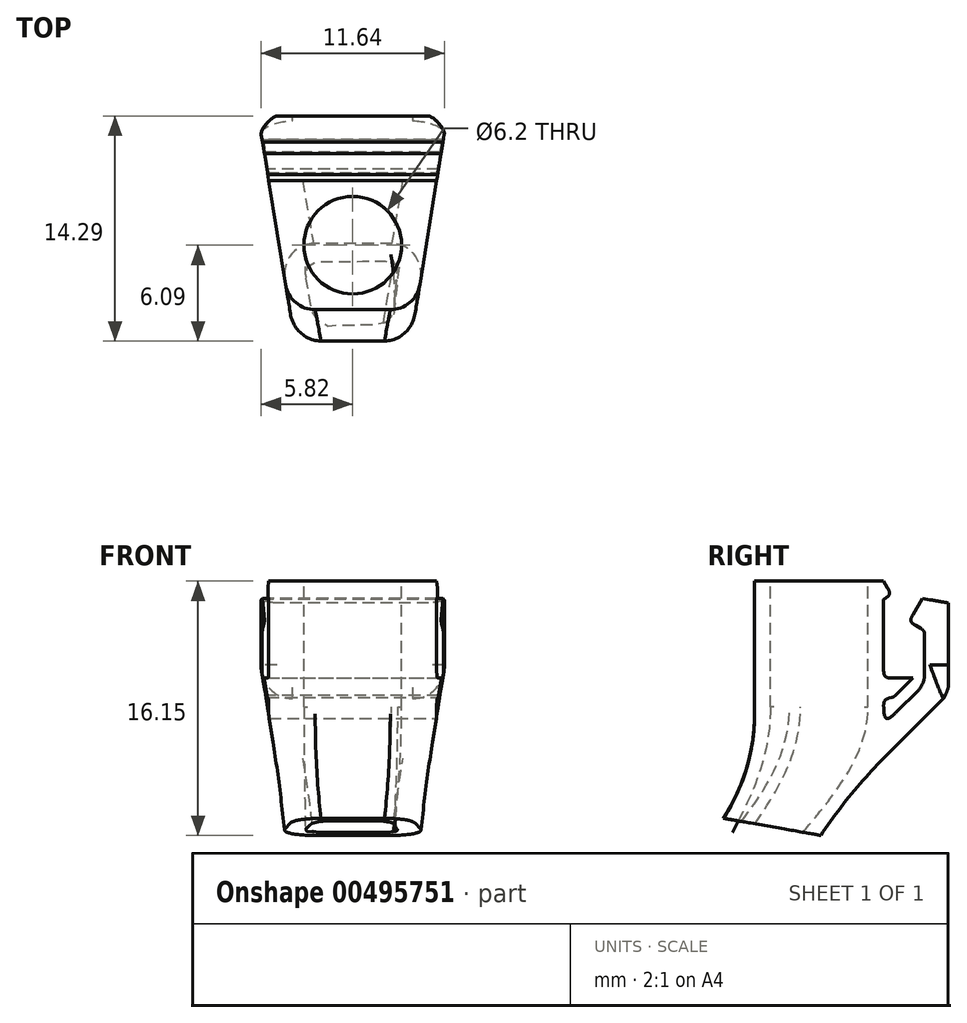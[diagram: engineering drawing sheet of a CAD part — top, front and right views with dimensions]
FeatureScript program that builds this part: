
annotation { "Feature Type Name" : "Feature", "Feature Type Description" : "" }
export const myFeature = defineFeature(function(context is Context, id is Id, definition is map)
    precondition{}
    {
        {
            var Q0;
            Q0=qCreatedBy(makeId("Right.planeOp"),FACE);
            var sketch = newSketch(context, id + "F0", { "sketchPlane" : qUnion([Q0])});
            skLineSegment(sketch, "E0", {"start": v(0, 0) * mm, "end": v(7, 0) * mm});
            skLineSegment(sketch, "E1", {"start": v(15.1, 9) * mm, "end": v(15.1, 14.77) * mm});
            skLineSegment(sketch, "E2", {"start": v(13.45, 15.06) * mm, "end": v(12.6, 13.58) * mm});
            skLineSegment(sketch, "E3", {"start": v(12.6, 13.58) * mm, "end": v(13.6, 13) * mm});
            skLineSegment(sketch, "E4", {"start": v(13.6, 13) * mm, "end": v(13.6, 10) * mm});
            skLineSegment(sketch, "E5", {"start": v(13.6, 10) * mm, "end": v(11, 10) * mm});
            skLineSegment(sketch, "E6", {"start": v(11, 10) * mm, "end": v(11, 15) * mm});
            skLineSegment(sketch, "E7", {"start": v(11, 15) * mm, "end": v(11.5, 15.29) * mm});
            skLineSegment(sketch, "E8", {"start": v(11.5, 15.29) * mm, "end": v(11, 16.15) * mm});
            skLineSegment(sketch, "E9", {"start": v(11, 16.15) * mm, "end": v(2.8, 16.15) * mm});
            skLineSegment(sketch, "E10", {"start": v(2.8, 16.15) * mm, "end": v(0, 0) * mm, "construction": true});
            skLineSegment(sketch, "E11", {"start": v(2.8, 16.15) * mm, "end": v(2.8, 7.7) * mm});
            skArc(sketch, "E12", {"start": v(0, 0) * mm, "mid": v(2.08, 3.6) * mm, "end": v(2.8, 7.7) * mm});
            skLineSegment(sketch, "E13", {"start": v(15.1, 9) * mm, "end": v(11, 4.9) * mm});
            skArc(sketch, "E14", {"start": v(7, 0) * mm, "mid": v(8.88, 2.54) * mm, "end": v(11, 4.9) * mm});
            skLineSegment(sketch, "E15", {"start": v(13.45, 15.06) * mm, "end": v(15.1, 14.77) * mm});
            skSolve(sketch);
        }
        {
            var Q0;
            Q0=qSketchRegion(id+"F0",true);
            extrude(context, id + "F1", {"entities" : qUnion([Q0]), "endBound" : BoundingType.SYMMETRIC, "depth" : 12 * mm});
        }
        {
            var Q0;
            Q0=qCreatedBy(makeId("Right.planeOp"),FACE);
            var sketch = newSketch(context, id + "F2", { "sketchPlane" : qUnion([Q0])});
            skLineSegment(sketch, "E16", {"start": v(13.6, 9.62) * mm, "end": v(11, 7.02) * mm});
            skLineSegment(sketch, "E17", {"start": v(11, 7.02) * mm, "end": v(11, 8.63) * mm});
            skLineSegment(sketch, "E18", {"start": v(11, 8.63) * mm, "end": v(11.65, 8.8) * mm});
            skLineSegment(sketch, "E19", {"start": v(11.65, 8.8) * mm, "end": v(12.85, 10) * mm});
            skLineSegment(sketch, "E20", {"start": v(12.85, 10) * mm, "end": v(13.6, 10) * mm});
            skLineSegment(sketch, "E21", {"start": v(13.6, 9.62) * mm, "end": v(13.6, 10) * mm});
            skSolve(sketch);
        }
        {
            var Q0;
            Q0=qSketchRegion(id+"F2",true);
            extrude(context, id + "F3", {"entities" : qUnion([Q0]), "operationType" : NewBodyOperationType.REMOVE, "endBound" : BoundingType.THROUGH_ALL, "oppositeDirection" : true, "depth" : 25 * mm, "hasSecondDirection" : true, "secondDirectionBound" : SecondDirectionBoundingType.THROUGH_ALL, "secondDirectionOppositeDirection" : false, "secondDirectionDepth" : 25 * mm});
        }
        {
            var Q0;
            Q0=makeQuery(id+"F1.opExtrude","SWEPT_FACE",FACE,{"disambiguationData":[OSD([sQuery(id+"F0.wireOp",EDGE,"E9")])]});
            var sketch = newSketch(context, id + "F4", { "sketchPlane" : qUnion([Q0])});
            skLineSegment(sketch, "E22", {"start": v(-6, 15.1) * mm, "end": v(-4, 2.8) * mm});
            skLineSegment(sketch, "E23", {"start": v(-4, 2.8) * mm, "end": v(-6, 2.8) * mm});
            skLineSegment(sketch, "E24", {"start": v(-6, 2.8) * mm, "end": v(-6, 15.1) * mm});
            skLineSegment(sketch, "E25", {"start": v(6, 2.8) * mm, "end": v(4, 2.8) * mm});
            skLineSegment(sketch, "E26", {"start": v(4, 2.8) * mm, "end": v(6, 15.1) * mm});
            skLineSegment(sketch, "E27", {"start": v(6, 15.1) * mm, "end": v(6, 2.8) * mm});
            skLineSegment(sketch, "E28", {"start": v(-4, 2.8) * mm, "end": v(-3.54, 0) * mm});
            skLineSegment(sketch, "E29", {"start": v(-3.54, 0) * mm, "end": v(-6, 0) * mm});
            skLineSegment(sketch, "E30", {"start": v(-6, 0) * mm, "end": v(-6, 2.8) * mm});
            skLineSegment(sketch, "E31", {"start": v(6, 2.8) * mm, "end": v(6, 0) * mm});
            skLineSegment(sketch, "E32", {"start": v(6, 0) * mm, "end": v(3.54, 0) * mm});
            skLineSegment(sketch, "E33", {"start": v(3.54, 0) * mm, "end": v(4, 2.8) * mm});
            skSolve(sketch);
        }
        {
            var Q0;
            Q0=qSketchRegion(id+"F4",true);
            extrude(context, id + "F5", {"entities" : qUnion([Q0]), "operationType" : NewBodyOperationType.REMOVE, "endBound" : BoundingType.THROUGH_ALL, "oppositeDirection" : true, "depth" : 25 * mm});
        }
        {
            var Q0;
            Q0=makeQuery(id+"F5.boolean.opBoolean","INTERSECT",EDGE,{"derivedFrom":[makeQuery(id+"F1.opExtrude","SWEPT_FACE",FACE,{"disambiguationData":[OSD([sQuery(id+"F0.wireOp",EDGE,"E14")])]}),makeQuery(id+"F5.opExtrude","SWEPT_FACE",FACE,{"disambiguationData":[OSD([sQuery(id+"F4.wireOp",EDGE,"E22"),sQuery(id+"F4.wireOp",EDGE,"E28")])]})]});
            var Q1;
            Q1=makeQuery(id+"F5.boolean.opBoolean","INTERSECT",EDGE,{"derivedFrom":[makeQuery(id+"F1.opExtrude","SWEPT_FACE",FACE,{"disambiguationData":[OSD([sQuery(id+"F0.wireOp",EDGE,"E12")])]}),makeQuery(id+"F5.opExtrude","SWEPT_FACE",FACE,{"disambiguationData":[OSD([sQuery(id+"F4.wireOp",EDGE,"E22"),sQuery(id+"F4.wireOp",EDGE,"E28")])]})]});
            var Q2;
            Q2=makeQuery(id+"F5.boolean.opBoolean","INTERSECT",EDGE,{"derivedFrom":[makeQuery(id+"F1.opExtrude","SWEPT_FACE",FACE,{"disambiguationData":[OSD([sQuery(id+"F0.wireOp",EDGE,"E14")])]}),makeQuery(id+"F5.opExtrude","SWEPT_FACE",FACE,{"disambiguationData":[OSD([sQuery(id+"F4.wireOp",EDGE,"E26"),sQuery(id+"F4.wireOp",EDGE,"E33")])]})]});
            var Q3;
            Q3=makeQuery(id+"F5.boolean.opBoolean","INTERSECT",EDGE,{"derivedFrom":[makeQuery(id+"F1.opExtrude","SWEPT_FACE",FACE,{"disambiguationData":[OSD([sQuery(id+"F0.wireOp",EDGE,"E12")])]}),makeQuery(id+"F5.opExtrude","SWEPT_FACE",FACE,{"disambiguationData":[OSD([sQuery(id+"F4.wireOp",EDGE,"E26"),sQuery(id+"F4.wireOp",EDGE,"E33")])]})]});
            fillet(context, id + "F6", {"entities" : qUnion([Q0, Q1, Q2, Q3]), "radius" : 1.9 * mm, "tangentPropagation" : true, "allowEdgeOverflow" : false});
        }
        {
            var Q0;
            Q0=makeQuery(id+"F1.opExtrude","SWEPT_FACE",FACE,{"disambiguationData":[OSD([sQuery(id+"F0.wireOp",EDGE,"E0")])]});
            var sketch = newSketch(context, id + "F7", { "sketchPlane" : qUnion([Q0])});
            skFitSpline(sketch, "E34.0", {"points": [v(-2.98, -4.65) * mm, v(-3, -4.72) * mm, v(-3, -4.83) * mm, v(-3, -4.98) * mm, v(-2.98, -5.12) * mm, v(-2.93, -5.3) * mm, v(-2.87, -5.43) * mm, v(-2.8, -5.53) * mm, v(-2.74, -5.6) * mm, v(-2.65, -5.66) * mm, v(-2.58, -5.7) * mm, v(-2.53, -5.7) * mm, v(-2.5, -5.7) * mm]});
            skLineSegment(sketch, "E34.1", {"start": v(2.5, -5.7) * mm, "end": v(-2.5, -5.7) * mm});
            skLineSegment(sketch, "E34.2", {"start": v(-2.98, -4.65) * mm, "end": v(-2.6, -2.27) * mm});
            skFitSpline(sketch, "E34.3", {"points": [v(2.5, -5.7) * mm, v(2.53, -5.7) * mm, v(2.56, -5.7) * mm, v(2.62, -5.68) * mm, v(2.67, -5.65) * mm, v(2.75, -5.58) * mm, v(2.88, -5.42) * mm, v(3, -5.1) * mm, v(3, -4.8) * mm, v(2.98, -4.65) * mm]});
            skFitSpline(sketch, "E34.4", {"points": [v(-1.84, -1.3) * mm, v(-1.85, -1.3) * mm, v(-1.88, -1.3) * mm, v(-1.96, -1.33) * mm, v(-2.04, -1.38) * mm, v(-2.13, -1.45) * mm, v(-2.25, -1.56) * mm, v(-2.38, -1.74) * mm, v(-2.52, -2) * mm, v(-2.59, -2.22) * mm, v(-2.61, -2.37) * mm]});
            skLineSegment(sketch, "E34.5", {"start": v(1.86, -1.3) * mm, "end": v(-1.86, -1.3) * mm});
            skFitSpline(sketch, "E34.6", {"points": [v(2.61, -2.37) * mm, v(2.6, -2.3) * mm, v(2.57, -2.15) * mm, v(2.49, -1.94) * mm, v(2.37, -1.73) * mm, v(2.25, -1.57) * mm, v(2.1, -1.43) * mm, v(1.98, -1.34) * mm, v(1.87, -1.3) * mm, v(1.85, -1.3) * mm, v(1.84, -1.3) * mm]});
            skLineSegment(sketch, "E34.7", {"start": v(2.6, -2.27) * mm, "end": v(2.98, -4.65) * mm});
            skSolve(sketch);
        }
        {
            var Q0;
            Q0=makeQuery(id+"F1.opExtrude","SWEPT_FACE",FACE,{"disambiguationData":[OSD([sQuery(id+"F0.wireOp",EDGE,"E9")])]});
            var sketch = newSketch(context, id + "F8", { "sketchPlane" : qUnion([Q0])});
            skLineSegment(sketch, "E35", {"start": v(0, 11) * mm, "end": v(0, 11) * mm});
            skCircle(sketch, "E36", {"center": v(0, 6.9) * mm, "radius": 3.1 * mm});
            skLineSegment(sketch, "E37", {"start": v(0, 11) * mm, "end": v(0, 10) * mm, "construction": true});
            skLineSegment(sketch, "E38", {"start": v(0, 10) * mm, "end": v(0, 10) * mm});
            skLineSegment(sketch, "E39", {"start": v(0, 2.8) * mm, "end": v(0, 3.8) * mm, "construction": true});
            skSolve(sketch);
        }
        {
            var Q0;
            Q0=makeQuery(id+"F8.imprint","IMPRINT",FACE,{"disambiguationData":[TD([[makeQuery(id+"F8.imprint","IMPRINT",EDGE,{"derivedFrom":sQuery(id+"F8.wireOp",EDGE,"E36")}),1.0]])]});
            var Q1;
            Q1=sQuery(id+"F8.wireOp",EDGE,"E36");
            extrude(context, id + "F9", {"entities" : qUnion([Q0]), "operationType" : NewBodyOperationType.REMOVE, "surfaceEntities" : qUnion([Q1]), "oppositeDirection" : true, "depth" : 8 * mm});
        }
        {
            var Q0;
            Q0=makeQuery(id+"F9.boolean.opBoolean","COPY",FACE,{"derivedFrom":makeQuery(id+"F9.opExtrude","CAP_FACE",FACE,{"disambiguationData":[OSD([sQuery(id+"F8.wireOp",EDGE,"E36")])],"isStart":false})});
            var sketch = newSketch(context, id + "F10", { "sketchPlane" : qUnion([Q0])});
            skArc(sketch, "E40", {"start": v(1.19, 9.76) * mm, "mid": v(0, 10) * mm, "end": v(-1.19, 9.76) * mm});
            skLineSegment(sketch, "E41", {"start": v(-1.19, 9.76) * mm, "end": v(0, 6.9) * mm, "construction": true});
            skLineSegment(sketch, "E42", {"start": v(0, 6.9) * mm, "end": v(1.19, 9.76) * mm, "construction": true});
            skLineSegment(sketch, "E43", {"start": v(0, 6.9) * mm, "end": v(0, 10) * mm, "construction": true});
            skArc(sketch, "E44.1.0", {"start": v(-1.19, 9.76) * mm, "mid": v(-2.2, 9.1) * mm, "end": v(-2.86, 8.09) * mm});
            skArc(sketch, "E44.2.0", {"start": v(-2.86, 8.09) * mm, "mid": v(-3.1, 6.9) * mm, "end": v(-2.86, 5.71) * mm});
            skArc(sketch, "E44.3.0", {"start": v(-2.86, 5.71) * mm, "mid": v(-2.2, 4.7) * mm, "end": v(-1.19, 4.04) * mm});
            skArc(sketch, "E44.4.0", {"start": v(-1.19, 4.04) * mm, "mid": v(0, 3.8) * mm, "end": v(1.19, 4.04) * mm});
            skArc(sketch, "E44.5.0", {"start": v(1.19, 4.04) * mm, "mid": v(2.2, 4.7) * mm, "end": v(2.86, 5.71) * mm});
            skArc(sketch, "E44.6.0", {"start": v(2.86, 5.71) * mm, "mid": v(3.1, 6.9) * mm, "end": v(2.86, 8.09) * mm});
            skArc(sketch, "E44.7.0", {"start": v(2.86, 8.09) * mm, "mid": v(2.2, 9.1) * mm, "end": v(1.19, 9.76) * mm});
            skSolve(sketch);
        }
        {
            var Q1;
            Q1=qSketchRegion(id+"F7",true);
            var Q2;
            Q2=qSketchRegion(id+"F10",true);
            loft(context, id + "F11", {"operationType" : NewBodyOperationType.REMOVE, "endCondition" : LoftEndDerivativeType.NORMAL_TO_PROFILE, "endMagnitude" : 1.2, "sheetProfilesArray" : [{ "sheetProfileEntities" : qUnion([Q1]) }, { "sheetProfileEntities" : qUnion([Q2]) }]});
        }
        {
            var Q0;
            Q0=makeQuery(id+"F5.boolean.opBoolean","MERGE",EDGE,{"derivedFrom":[makeQuery(id+"F1.opExtrude","CAP_EDGE",EDGE,{"disambiguationData":[OSD([sQuery(id+"F0.wireOp",EDGE,"E1")])],"isStart":true}),makeQuery(id+"F5.opExtrude","SWEPT_EDGE",EDGE,{"disambiguationData":[OSD([sQuery(id+"F4.wireOp",EDGE,"E22"),sQuery(id+"F4.wireOp",EDGE,"E24")])]})]});
            fillet(context, id + "F12", {"entities" : qUnion([Q0]), "radius" : 1 * mm, "tangentPropagation" : true, "rho" : .2, "crossSection" : FilletCrossSection.CONIC, "allowEdgeOverflow" : false});
        }
        {
            var Q0;
            Q0=makeQuery(id+"F3.boolean.opBoolean","COPY",EDGE,{"derivedFrom":makeQuery(id+"F3.opExtrude","SWEPT_EDGE",EDGE,{"disambiguationData":[OSD([sQuery(id+"F2.wireOp",EDGE,"E16"),sQuery(id+"F2.wireOp",EDGE,"E17")])]})});
            var Q1;
            Q1=makeQuery(id+"F3.boolean.opBoolean","COPY",EDGE,{"derivedFrom":makeQuery(id+"F3.opExtrude","SWEPT_EDGE",EDGE,{"disambiguationData":[OSD([sQuery(id+"F2.wireOp",EDGE,"E17"),sQuery(id+"F2.wireOp",EDGE,"E18")])]})});
            var Q2;
            Q2=makeQuery(id+"F3.boolean.opBoolean","COPY",EDGE,{"derivedFrom":makeQuery(id+"F3.opExtrude","SWEPT_EDGE",EDGE,{"disambiguationData":[OSD([sQuery(id+"F2.wireOp",EDGE,"E18"),sQuery(id+"F2.wireOp",EDGE,"E19")])]})});
            var Q3;
            Q3=makeQuery(id+"F3.boolean.opBoolean","COPY",EDGE,{"derivedFrom":makeQuery(id+"F3.opExtrude","SWEPT_EDGE",EDGE,{"disambiguationData":[OSD([sQuery(id+"F2.wireOp",EDGE,"E19"),sQuery(id+"F2.wireOp",EDGE,"E20")])]})});
            var Q4;
            Q4=makeQuery(id+"F1.opExtrude","SWEPT_EDGE",EDGE,{"disambiguationData":[OSD([sQuery(id+"F0.wireOp",EDGE,"E5"),sQuery(id+"F0.wireOp",EDGE,"E6")])]});
            var Q5;
            Q5=makeQuery(id+"F1.opExtrude","SWEPT_EDGE",EDGE,{"disambiguationData":[OSD([sQuery(id+"F0.wireOp",EDGE,"E2"),sQuery(id+"F0.wireOp",EDGE,"E3")])]});
            var Q6;
            Q6=makeQuery(id+"F1.opExtrude","SWEPT_EDGE",EDGE,{"disambiguationData":[OSD([sQuery(id+"F0.wireOp",EDGE,"E3"),sQuery(id+"F0.wireOp",EDGE,"E4")])]});
            var Q7;
            Q7=makeQuery(id+"F1.opExtrude","SWEPT_EDGE",EDGE,{"disambiguationData":[OSD([sQuery(id+"F0.wireOp",EDGE,"E7"),sQuery(id+"F0.wireOp",EDGE,"E8")])]});
            fillet(context, id + "F13", {"entities" : qUnion([Q0, Q1, Q2, Q3, Q4, Q5, Q6, Q7]), "radius" : .5 * mm, "tangentPropagation" : true, "rho" : .6, "crossSection" : FilletCrossSection.CONIC, "allowEdgeOverflow" : false});
        }
        {
            var Q0;
            Q0=makeQuery(id+"F3.boolean.opBoolean","COPY",EDGE,{"derivedFrom":makeQuery(id+"F3.opExtrude","SWEPT_EDGE",EDGE,{"disambiguationData":[OSD([sQuery(id+"F2.wireOp",EDGE,"E16"),sQuery(id+"F2.wireOp",EDGE,"E21")])]})});
            fillet(context, id + "F14", {"entities" : qUnion([Q0]), "radius" : 1.5 * mm, "tangentPropagation" : true, "allowEdgeOverflow" : false});
        }
        {
            var Q0;
            Q0=qCreatedBy(makeId("Right.planeOp"),FACE);
            var sketch = newSketch(context, id + "F15", { "sketchPlane" : qUnion([Q0])});
            skLineSegment(sketch, "E45", {"start": v(7, 0) * mm, "end": v(0, 0) * mm});
            skLineSegment(sketch, "E46", {"start": v(0, 0) * mm, "end": v(0, 1.23) * mm});
            skLineSegment(sketch, "E47", {"start": v(0, 1.23) * mm, "end": v(7, 0) * mm});
            skSolve(sketch);
        }
        {
            var Q0;
            Q0=qSketchRegion(id+"F15",true);
            extrude(context, id + "F16", {"entities" : qUnion([Q0]), "operationType" : NewBodyOperationType.REMOVE, "endBound" : BoundingType.THROUGH_ALL, "oppositeDirection" : true, "depth" : 25 * mm, "hasSecondDirection" : true, "secondDirectionBound" : SecondDirectionBoundingType.THROUGH_ALL, "secondDirectionOppositeDirection" : false, "secondDirectionDepth" : 25 * mm});
        }
    });
